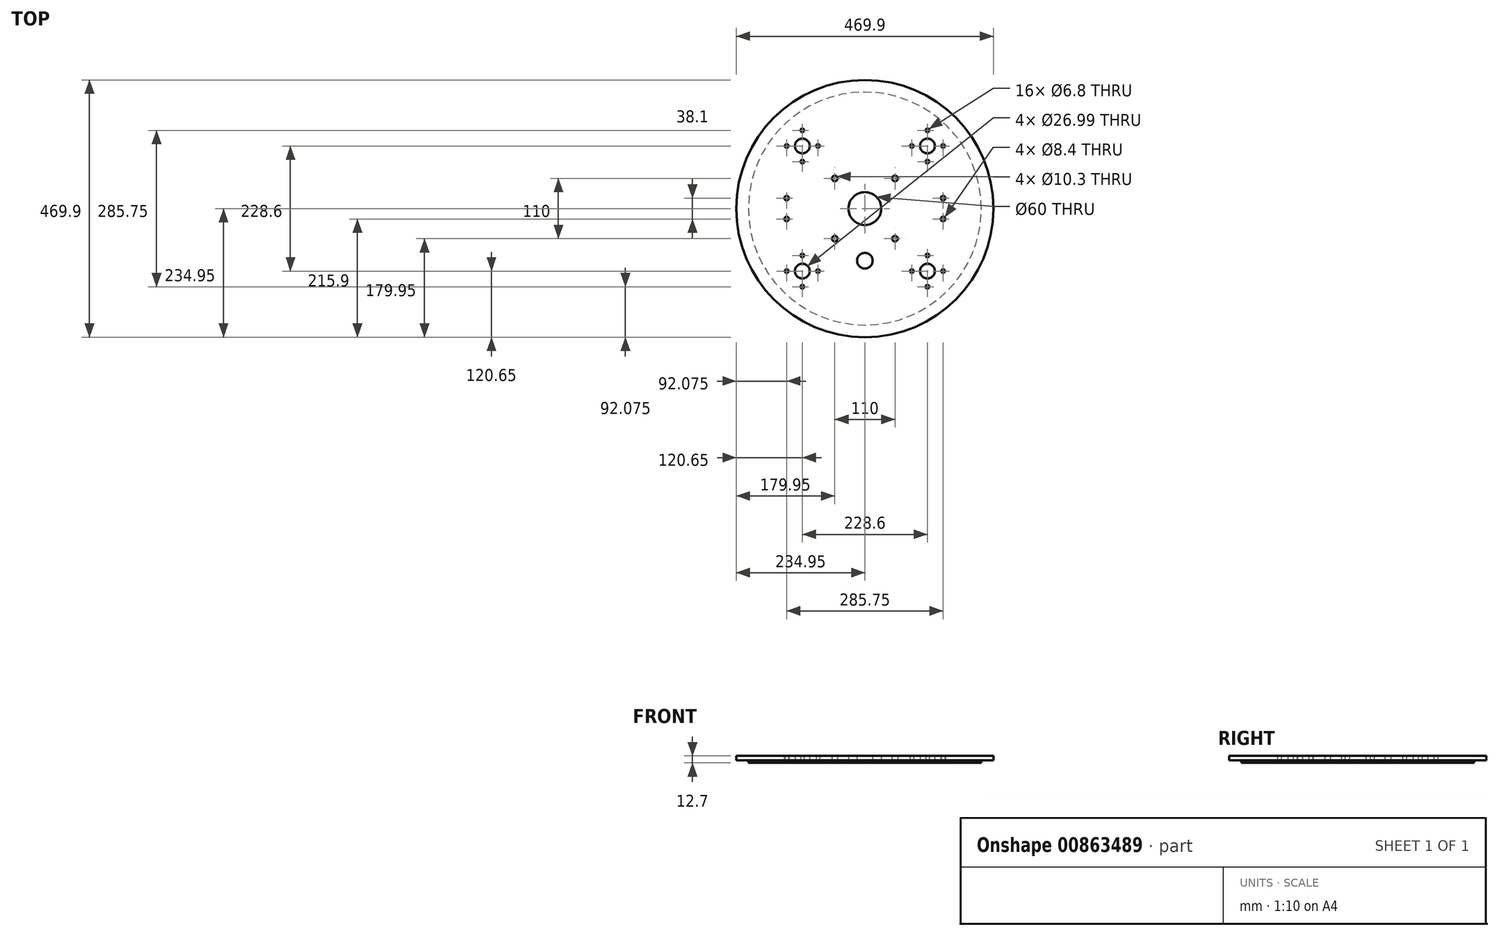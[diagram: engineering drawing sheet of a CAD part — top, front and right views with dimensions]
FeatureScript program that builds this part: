
annotation { "Feature Type Name" : "Feature", "Feature Type Description" : "" }
export const myFeature = defineFeature(function(context is Context, id is Id, definition is map)
    precondition{}
    {
        {
            var Q0;
            Q0=qCreatedBy(makeId("Top.planeOp"),FACE);
            var sketch = newSketch(context, id + "F0", { "sketchPlane" : qUnion([Q0])});
            skCircle(sketch, "E0", {"center": v(0, 0) * mm, "radius": 234.95 * mm});
            skCircle(sketch, "E1", {"center": v(-114.3, -114.3) * mm, "radius": 13.5 * mm});
            skCircle(sketch, "E2", {"center": v(0, 0) * mm, "radius": 30 * mm});
            skCircle(sketch, "E3", {"center": v(0, -95.25) * mm, "radius": 14.29 * mm});
            skPoint(sketch, "E4", {"position": v(-114.3, -142.88) * mm});
            skPoint(sketch, "E5.1.0", {"position": v(-85.72, -114.3) * mm});
            skPoint(sketch, "E5.2.0", {"position": v(-114.3, -85.73) * mm});
            skPoint(sketch, "E5.3.0", {"position": v(-142.88, -114.3) * mm});
            skPoint(sketch, "E6", {"position": v(-55, -55) * mm});
            skPoint(sketch, "E7", {"position": v(-142.88, -19.05) * mm});
            skPoint(sketch, "E8", {"position": v(-142.88, 19.05) * mm});
            skPoint(sketch, "E9.MirrorP", {"position": v(142.88, -19.05) * mm});
            skPoint(sketch, "E10.MirrorP", {"position": v(142.88, 19.05) * mm});
            skPoint(sketch, "E11.1.0", {"position": v(55, -55) * mm});
            skPoint(sketch, "E11.1.1", {"position": v(114.3, -85.73) * mm});
            skPoint(sketch, "E11.1.2", {"position": v(85.73, -114.3) * mm});
            skPoint(sketch, "E11.1.3", {"position": v(114.3, -142.88) * mm});
            skPoint(sketch, "E11.1.4", {"position": v(142.88, -114.3) * mm});
            skCircle(sketch, "E11.1.5", {"center": v(114.3, -114.3) * mm, "radius": 13.5 * mm});
            skPoint(sketch, "E11.2.0", {"position": v(55, 55) * mm});
            skPoint(sketch, "E11.2.1", {"position": v(85.73, 114.3) * mm});
            skPoint(sketch, "E11.2.2", {"position": v(114.3, 85.73) * mm});
            skPoint(sketch, "E11.2.3", {"position": v(142.88, 114.3) * mm});
            skPoint(sketch, "E11.2.4", {"position": v(114.3, 142.88) * mm});
            skCircle(sketch, "E11.2.5", {"center": v(114.3, 114.3) * mm, "radius": 13.5 * mm});
            skPoint(sketch, "E11.3.0", {"position": v(-55, 55) * mm});
            skPoint(sketch, "E11.3.1", {"position": v(-114.3, 85.73) * mm});
            skPoint(sketch, "E11.3.2", {"position": v(-85.73, 114.3) * mm});
            skPoint(sketch, "E11.3.3", {"position": v(-114.3, 142.88) * mm});
            skPoint(sketch, "E11.3.4", {"position": v(-142.88, 114.3) * mm});
            skCircle(sketch, "E11.3.5", {"center": v(-114.3, 114.3) * mm, "radius": 13.5 * mm});
            skSolve(sketch);
        }
        {
            var Q0;
            Q0=makeQuery(id+"F0.imprint","IMPRINT",FACE,{"disambiguationData":[TD([[makeQuery(id+"F0.imprint","IMPRINT",EDGE,{"derivedFrom":sQuery(id+"F0.wireOp",EDGE,"E0")}),1.0]])]});
            var Q1;
            Q1=sQuery(id+"F0.wireOp",EDGE,"E0");
            extrude(context, id + "F1", {"entities" : qUnion([Q0]), "surfaceEntities" : qUnion([Q1]), "depth" : 12.7 * mm, "offsetDistance" : 25.4 * mm});
        }
        {
            var Q0;
            Q0=sQuery(id+"F0.wireOp",VERTEX,"E5.2.0");
            var Q1;
            Q1=sQuery(id+"F0.wireOp",VERTEX,"E5.1.0");
            var Q2;
            Q2=sQuery(id+"F0.wireOp",VERTEX,"E5.3.0");
            var Q3;
            Q3=sQuery(id+"F0.wireOp",VERTEX,"E4");
            var Q4;
            Q4=sQuery(id+"F0.wireOp",VERTEX,"E11.3.4");
            var Q5;
            Q5=sQuery(id+"F0.wireOp",VERTEX,"E11.3.3");
            var Q6;
            Q6=sQuery(id+"F0.wireOp",VERTEX,"E11.3.2");
            var Q7;
            Q7=sQuery(id+"F0.wireOp",VERTEX,"E11.3.1");
            var Q8;
            Q8=sQuery(id+"F0.wireOp",VERTEX,"E11.2.4");
            var Q9;
            Q9=sQuery(id+"F0.wireOp",VERTEX,"E11.2.3");
            var Q10;
            Q10=sQuery(id+"F0.wireOp",VERTEX,"E11.2.1");
            var Q11;
            Q11=sQuery(id+"F0.wireOp",VERTEX,"E11.2.2");
            var Q12;
            Q12=sQuery(id+"F0.wireOp",VERTEX,"E11.1.2");
            var Q13;
            Q13=sQuery(id+"F0.wireOp",VERTEX,"E11.1.1");
            var Q14;
            Q14=sQuery(id+"F0.wireOp",VERTEX,"E11.1.4");
            var Q15;
            Q15=sQuery(id+"F0.wireOp",VERTEX,"E11.1.3");
            var Q16;
            Q16=makeQuery(id+"F1.opExtrude","SWEPT_BODY",BODY,{"disambiguationData":[OSD([sQuery(id+"F0.wireOp",EDGE,"E0"),sQuery(id+"F0.wireOp",EDGE,"E1"),sQuery(id+"F0.wireOp",EDGE,"E2"),sQuery(id+"F0.wireOp",EDGE,"E3"),sQuery(id+"F0.wireOp",EDGE,"E11.1.5"),sQuery(id+"F0.wireOp",EDGE,"E11.2.5"),sQuery(id+"F0.wireOp",EDGE,"E11.3.5")])]});
            hole(context, id + "F2", {"style" : HoleStyle.SIMPLE, "endStyle" : HoleEndStyle.THROUGH, "oppositeDirection" : true, "standardTappedOrClearance" : lookupTablePath({ "standard" : "ISO", "engagement" : "75%", "pitch" : "1.25 mm", "size" : "M8", "type" : "Tapped" }), "standardBlindInLast" : lookupTablePath({ "standard" : "ISO", "engagement" : "75%", "pitch" : "1.25 mm", "size" : "M8", "type" : "Tapped" }), "holeDiameter" : 6.8 * mm, "majorDiameter" : 8 * mm, "showTappedDepth" : true, "isTappedThrough" : true, "tappedDepth" : 12.7 * mm, "tapClearance" : 3, "locations" : qUnion([Q0, Q1, Q2, Q3, Q4, Q5, Q6, Q7, Q8, Q9, Q10, Q11, Q12, Q13, Q14, Q15]), "scope" : qUnion([Q16])});
        }
        {
            var Q0;
            Q0=sQuery(id+"F0.wireOp",VERTEX,"E7");
            var Q1;
            Q1=sQuery(id+"F0.wireOp",VERTEX,"E8");
            var Q2;
            Q2=sQuery(id+"F0.wireOp",VERTEX,"E10.MirrorP");
            var Q3;
            Q3=sQuery(id+"F0.wireOp",VERTEX,"E9.MirrorP");
            var Q4;
            Q4=makeQuery(id+"F1.opExtrude","SWEPT_BODY",BODY,{"disambiguationData":[OSD([sQuery(id+"F0.wireOp",EDGE,"E0"),sQuery(id+"F0.wireOp",EDGE,"E1"),sQuery(id+"F0.wireOp",EDGE,"E2"),sQuery(id+"F0.wireOp",EDGE,"E3"),sQuery(id+"F0.wireOp",EDGE,"E11.1.5"),sQuery(id+"F0.wireOp",EDGE,"E11.2.5"),sQuery(id+"F0.wireOp",EDGE,"E11.3.5")])]});
            hole(context, id + "F3", {"style" : HoleStyle.SIMPLE, "endStyle" : HoleEndStyle.THROUGH, "oppositeDirection" : true, "standardTappedOrClearance" : lookupTablePath({ "fit" : "Close", "standard" : "ISO", "size" : "M8", "type" : "Clearance" }), "standardBlindInLast" : lookupTablePath({ "fit" : "Close", "standard" : "ISO", "size" : "M8", "type" : "Clearance" }), "holeDiameter" : 8.4 * mm, "majorDiameter" : 8 * mm, "isTappedThrough" : true, "tappedDepth" : 12.7 * mm, "tapClearance" : 3, "locations" : qUnion([Q0, Q1, Q2, Q3]), "scope" : qUnion([Q4])});
        }
        {
            var Q0;
            Q0=sQuery(id+"F0.wireOp",VERTEX,"E6");
            var Q1;
            Q1=sQuery(id+"F0.wireOp",VERTEX,"E11.3.0");
            var Q2;
            Q2=sQuery(id+"F0.wireOp",VERTEX,"E11.2.0");
            var Q3;
            Q3=sQuery(id+"F0.wireOp",VERTEX,"E11.1.0");
            var Q4;
            Q4=makeQuery(id+"F1.opExtrude","SWEPT_BODY",BODY,{"disambiguationData":[OSD([sQuery(id+"F0.wireOp",EDGE,"E0"),sQuery(id+"F0.wireOp",EDGE,"E1"),sQuery(id+"F0.wireOp",EDGE,"E2"),sQuery(id+"F0.wireOp",EDGE,"E3"),sQuery(id+"F0.wireOp",EDGE,"E11.1.5"),sQuery(id+"F0.wireOp",EDGE,"E11.2.5"),sQuery(id+"F0.wireOp",EDGE,"E11.3.5")])]});
            hole(context, id + "F4", {"style" : HoleStyle.SIMPLE, "endStyle" : HoleEndStyle.THROUGH, "oppositeDirection" : true, "standardTappedOrClearance" : lookupTablePath({ "standard" : "ISO", "engagement" : "75%", "pitch" : "1.75 mm", "size" : "M12", "type" : "Tapped" }), "standardBlindInLast" : lookupTablePath({ "standard" : "ISO", "engagement" : "75%", "pitch" : "1.75 mm", "size" : "M12", "type" : "Tapped" }), "holeDiameter" : 10.3 * mm, "majorDiameter" : 12 * mm, "showTappedDepth" : true, "isTappedThrough" : true, "tappedDepth" : 12.7 * mm, "tapClearance" : 3, "locations" : qUnion([Q0, Q1, Q2, Q3]), "scope" : qUnion([Q4])});
        }
        {
            var Q0;
            Q0=makeQuery(id+"F0.imprint","IMPRINT",FACE,{"disambiguationData":[TD([[makeQuery(id+"F0.imprint","IMPRINT",EDGE,{"derivedFrom":sQuery(id+"F0.wireOp",EDGE,"E2")}),1.0]])]});
            var sketch = newSketch(context, id + "F5", { "sketchPlane" : qUnion([Q0])});
            skCircle(sketch, "E12", {"center": v(0, 0) * mm, "radius": 212.73 * mm});
            skCircle(sketch, "E13", {"center": v(0, 0) * mm, "radius": 295.37 * mm});
            skSolve(sketch);
        }
        {
            var Q0;
            Q0=makeQuery(id+"F5.imprint","IMPRINT",FACE,{"disambiguationData":[TD([[makeQuery(id+"F5.imprint","IMPRINT",EDGE,{"derivedFrom":sQuery(id+"F5.wireOp",EDGE,"E12")}),-1.0]])]});
            extrude(context, id + "F6", {"entities" : qUnion([Q0]), "operationType" : NewBodyOperationType.REMOVE, "depth" : 4.76 * mm, "offsetDistance" : 25.4 * mm});
        }
    });
